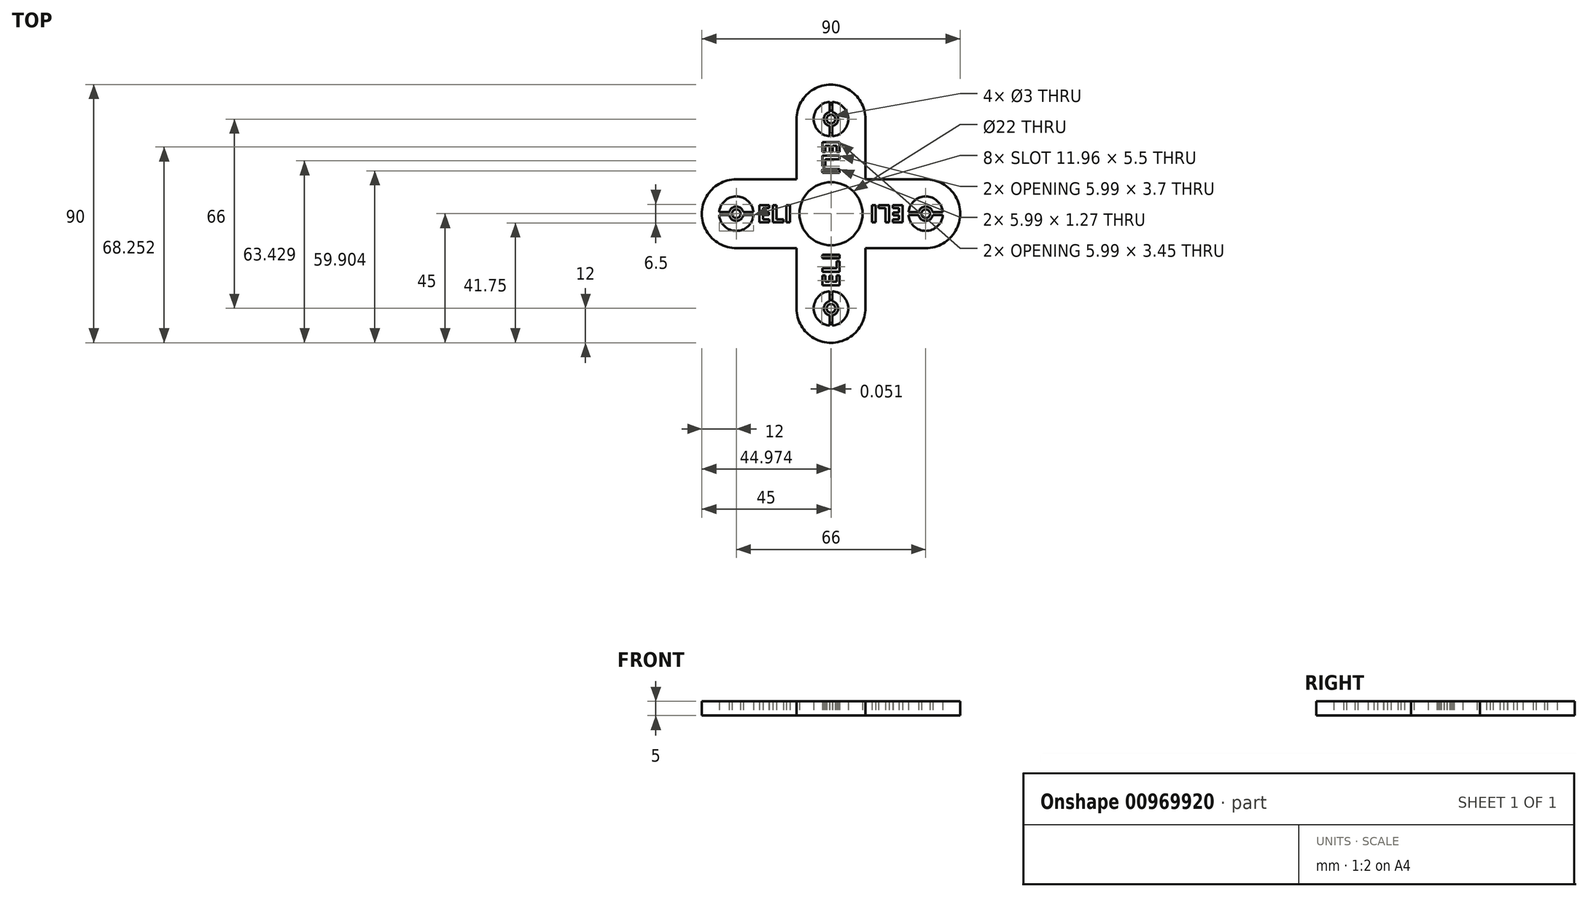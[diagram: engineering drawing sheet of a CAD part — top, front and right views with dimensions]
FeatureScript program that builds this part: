
annotation { "Feature Type Name" : "Feature", "Feature Type Description" : "" }
export const myFeature = defineFeature(function(context is Context, id is Id, definition is map)
    precondition{}
    {
        {
            var Q0;
            Q0=qCreatedBy(makeId("Top.planeOp"),FACE);
            var sketch = newSketch(context, id + "F0", { "sketchPlane" : qUnion([Q0])});
            skCircle(sketch, "E0", {"center": v(0, 0) * mm, "radius": 11 * mm});
            skCircle(sketch, "E1", {"center": v(0, 0) * mm, "radius": 45 * mm, "construction": true});
            skLineSegment(sketch, "E2.right", {"start": v(0, 12) * mm, "end": v(0, -12) * mm});
            skLineSegment(sketch, "E3.MirrorCS", {"start": v(-33, 12) * mm, "end": v(0, 12) * mm});
            skCircle(sketch, "E4.MirrorC", {"center": v(-33, 0) * mm, "radius": 12 * mm});
            skLineSegment(sketch, "E5.MirrorCS", {"start": v(-33, -12) * mm, "end": v(0, -12) * mm});
            skLineSegment(sketch, "E6", {"start": v(0, 0) * mm, "end": v(-33, 0) * mm});
            skCircle(sketch, "E7", {"center": v(-33, 0) * mm, "radius": 6 * mm});
            skCircle(sketch, "E8", {"center": v(-33, 0) * mm, "radius": 2.5 * mm});
            skCircle(sketch, "E9", {"center": v(-33, 0) * mm, "radius": 1.5 * mm});
            skLineSegment(sketch, "E10.bottom", {"start": v(-27.02, -0.5) * mm, "end": v(-30.55, -0.5) * mm});
            skLineSegment(sketch, "E10.top", {"start": v(-27.02, 0.5) * mm, "end": v(-30.55, 0.5) * mm});
            skLineSegment(sketch, "E11.trimOffspring", {"start": v(-35.45, 0.5) * mm, "end": v(-38.98, 0.5) * mm});
            skLineSegment(sketch, "E12.trimOffspring", {"start": v(-35.45, -0.5) * mm, "end": v(-38.98, -0.5) * mm});
            skPoint(sketch, "E13.orphan", {"position": v(-26, 0.5) * mm});
            skPoint(sketch, "E14.orphan", {"position": v(-26, -0.5) * mm});
            skPoint(sketch, "E10.right.end.orphan", {"position": v(-40, 0.5) * mm});
            skPoint(sketch, "E15.orphan", {"position": v(-40, -0.5) * mm});
            skText(sketch, "E16", { "text": "ELI", "fontName": "OpenSans-Bold.ttf"});
            skCircle(sketch, "E17", {"center": v(0, 0) * mm, "radius": 5.37 * mm, "construction": true});
            const initialGuessF0  = {"E16": [-0.02573, -0.00302, 1, 0, 0.00604]};
            skSetInitialGuess(sketch, initialGuessF0);
            skSolve(sketch);
        }
        {
            var Q0;
            {var subQ0=sQuery(id+"F0.wireOp",EDGE,"E11.trimOffspring");Q0=makeQuery(id+"F0.imprint","IMPRINT",FACE,{"disambiguationData":[TD([[makeQuery(id+"F0.imprint","IMPRINT",EDGE,{"derivedFrom":subQ0}),1.0]])]});}
            var Q1;
            {var subQ5=sQuery(id+"F0.wireOp",EDGE,"E10.bottom");Q1=makeQuery(id+"F0.imprint","IMPRINT",FACE,{"disambiguationData":[TD([[makeQuery(id+"F0.imprint","IMPRINT",EDGE,{"derivedFrom":subQ5}),-1.0]])]});}
            var Q2;
            {var subQ5=sQuery(id+"F0.wireOp",EDGE,"E10.top");Q2=makeQuery(id+"F0.imprint","IMPRINT",FACE,{"disambiguationData":[TD([[makeQuery(id+"F0.imprint","IMPRINT",EDGE,{"derivedFrom":subQ5}),1.0]])]});}
            var Q3;
            Q3=makeQuery(id+"F0.imprint","IMPRINT",FACE,{"disambiguationData":[TD([[makeQuery(id+"F0.imprint","IMPRINT",EDGE,{"derivedFrom":sQuery(id+"F0.wireOp",EDGE,"E9")}),-1.0]])]});
            var Q4;
            {var subQ0=sQuery(id+"F0.wireOp",EDGE,"E3.MirrorCS");Q4=makeQuery(id+"F0.imprint","IMPRINT",FACE,{"disambiguationData":[TD([[makeQuery(id+"F0.imprint","IMPRINT",EDGE,{"derivedFrom":subQ0}),-1.0]])]});}
            var Q5;
            {var subQ5=sQuery(id+"F0.wireOp",EDGE,"E2.right");var subQ7=sQuery(id+"F0.wireOp",EDGE,"E0");var subQ8=makeQuery(id+"F0.imprint","INTERSECT",VERTEX,{"disambiguationData":[OD(1.0)],"derivedFrom":[subQ7,subQ5]});Q5=makeQuery(id+"F0.imprint","IMPRINT",FACE,{"disambiguationData":[TD([[makeQuery(id+"F0.imprint","IMPRINT",EDGE,{"disambiguationData":[TD([[subQ8,1.0]])],"derivedFrom":subQ7}),-1.0]])]});}
            var Q6;
            {var subQ4=sQuery(id+"F0.wireOp",EDGE,"E4.MirrorC");var subQ7=makeQuery(id+"F0.imprint","INTERSECT",VERTEX,{"derivedFrom":[sQuery(id+"F0.wireOp",EDGE,"E3.MirrorCS"),subQ4]});Q6=makeQuery(id+"F0.imprint","IMPRINT",FACE,{"disambiguationData":[TD([[makeQuery(id+"F0.imprint","IMPRINT",EDGE,{"disambiguationData":[TD([[subQ7,1.0]])],"derivedFrom":subQ4}),1.0]])]});}
            var Q7;
            {var subQ0=sQuery(id+"F0.wireOp",EDGE,"E16.sketch_text.stroke-4");Q7=makeQuery(id+"F0.imprint","IMPRINT",FACE,{"disambiguationData":[TD([[makeQuery(id+"F0.imprint","IMPRINT",EDGE,{"derivedFrom":subQ0}),1.0]])]});}
            var Q8;
            {var subQ0=sQuery(id+"F0.wireOp",EDGE,"E16.sketch_text.stroke-8");Q8=makeQuery(id+"F0.imprint","IMPRINT",FACE,{"disambiguationData":[TD([[makeQuery(id+"F0.imprint","IMPRINT",EDGE,{"derivedFrom":subQ0}),1.0]])]});}
            extrude(context, id + "F1", {"entities" : qUnion([Q0, Q1, Q2, Q3, Q4, Q5, Q6, Q7, Q8]), "depth" : 5 * mm, "offsetDistance" : 25 * mm});
        }
        {
            var Q0;
            Q0=makeQuery(id+"F1.opExtrude","SWEPT_BODY",BODY,{"disambiguationData":[OSD([sQuery(id+"F0.wireOp",EDGE,"E0"),sQuery(id+"F0.wireOp",EDGE,"E2.right"),sQuery(id+"F0.wireOp",EDGE,"E3.MirrorCS"),sQuery(id+"F0.wireOp",EDGE,"E4.MirrorC"),sQuery(id+"F0.wireOp",EDGE,"E5.MirrorCS"),sQuery(id+"F0.wireOp",EDGE,"E7"),sQuery(id+"F0.wireOp",EDGE,"E8"),sQuery(id+"F0.wireOp",EDGE,"E9"),sQuery(id+"F0.wireOp",EDGE,"E10.bottom"),sQuery(id+"F0.wireOp",EDGE,"E10.top"),sQuery(id+"F0.wireOp",EDGE,"E11.trimOffspring"),sQuery(id+"F0.wireOp",EDGE,"E12.trimOffspring"),sQuery(id+"F0.wireOp",EDGE,"E16.sketch_text.stroke-0"),sQuery(id+"F0.wireOp",EDGE,"E16.sketch_text.stroke-1"),sQuery(id+"F0.wireOp",EDGE,"E16.sketch_text.stroke-2"),sQuery(id+"F0.wireOp",EDGE,"E16.sketch_text.stroke-3"),sQuery(id+"F0.wireOp",EDGE,"E16.sketch_text.stroke-4"),sQuery(id+"F0.wireOp",EDGE,"E16.sketch_text.stroke-5"),sQuery(id+"F0.wireOp",EDGE,"E16.sketch_text.stroke-6"),sQuery(id+"F0.wireOp",EDGE,"E16.sketch_text.stroke-7"),sQuery(id+"F0.wireOp",EDGE,"E16.sketch_text.stroke-8"),sQuery(id+"F0.wireOp",EDGE,"E16.sketch_text.stroke-9"),sQuery(id+"F0.wireOp",EDGE,"E16.sketch_text.stroke-10"),sQuery(id+"F0.wireOp",EDGE,"E16.sketch_text.stroke-11"),sQuery(id+"F0.wireOp",EDGE,"E16.sketch_text.stroke-12"),sQuery(id+"F0.wireOp",EDGE,"E16.sketch_text.stroke-13"),sQuery(id+"F0.wireOp",EDGE,"E16.sketch_text.stroke-14"),sQuery(id+"F0.wireOp",EDGE,"E16.sketch_text.stroke-15"),sQuery(id+"F0.wireOp",EDGE,"E16.sketch_text.stroke-16"),sQuery(id+"F0.wireOp",EDGE,"E16.sketch_text.stroke-17"),sQuery(id+"F0.wireOp",EDGE,"E16.sketch_text.stroke-18"),sQuery(id+"F0.wireOp",EDGE,"E16.sketch_text.stroke-19"),sQuery(id+"F0.wireOp",EDGE,"E16.sketch_text.stroke-20"),sQuery(id+"F0.wireOp",EDGE,"E16.sketch_text.stroke-21")])]});
            var Q1;
            Q1=makeQuery(id+"F1.opExtrude","CAP_EDGE",EDGE,{"disambiguationData":[OSD([sQuery(id+"F0.wireOp",EDGE,"E0")])],"isStart":false});
            circularPattern(context, id + "F2", {"operationType" : NewBodyOperationType.ADD, "entities" : qUnion([Q0]), "axis" : qUnion([Q1]), "angle" : 360 * degree, "instanceCount" : 4, "equalSpace" : true});
        }
    });
